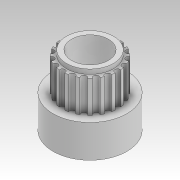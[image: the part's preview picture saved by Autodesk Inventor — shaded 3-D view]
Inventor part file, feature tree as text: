
AUTODESK INVENTOR PART (.ipt)
format: ipt  version: 2020 (Build 240168000, 168)  size: 196,608 bytes
history: native  units: mm
features: sketch x3, extrude x2, pattern_circular x2, revolve x1
ambient origin geometry x8: Origin, YZ Plane, XZ Plane, XY Plane, X Axis, Y Axis, Z Axis, Center Point
bodies: Solid1 (feature_tree)
feature tree (8):
  revolve  "Revolution1"  [1 undecoded]
  extrude  "Extrusion1"  Depth=6.11mm
  pattern_circular  "Circular Pattern1"  [2 undecoded]
  extrude  "Extrusion2"  TaperAngle=90.0deg  [1 undecoded]
  pattern_circular  "Circular Pattern2"  [2 undecoded]
  sketch  "Sketch1"  dims[d0=7.0mm d1=7.1mm]
  sketch  "Sketch2"  dims[d2=8.0mm d3=6.11mm]
  sketch  "Sketch3"  dims[d5=1.0mm d6=1.0mm d7=90.0deg d8=1.2mm d9=6.0mm d10=10.0mm d11=0.0mm d12=200.0mm d13=360.0deg d15=4.0mm d16=2.5mm d17=10.0mm d18=0.0mm d19=20.0mm d20=90.0deg]
note: 6 required parameter values undecoded (feature->parameter linkage not recoverable at this tier; creation-order binding heuristic only, values carry confidence <= 0.55)